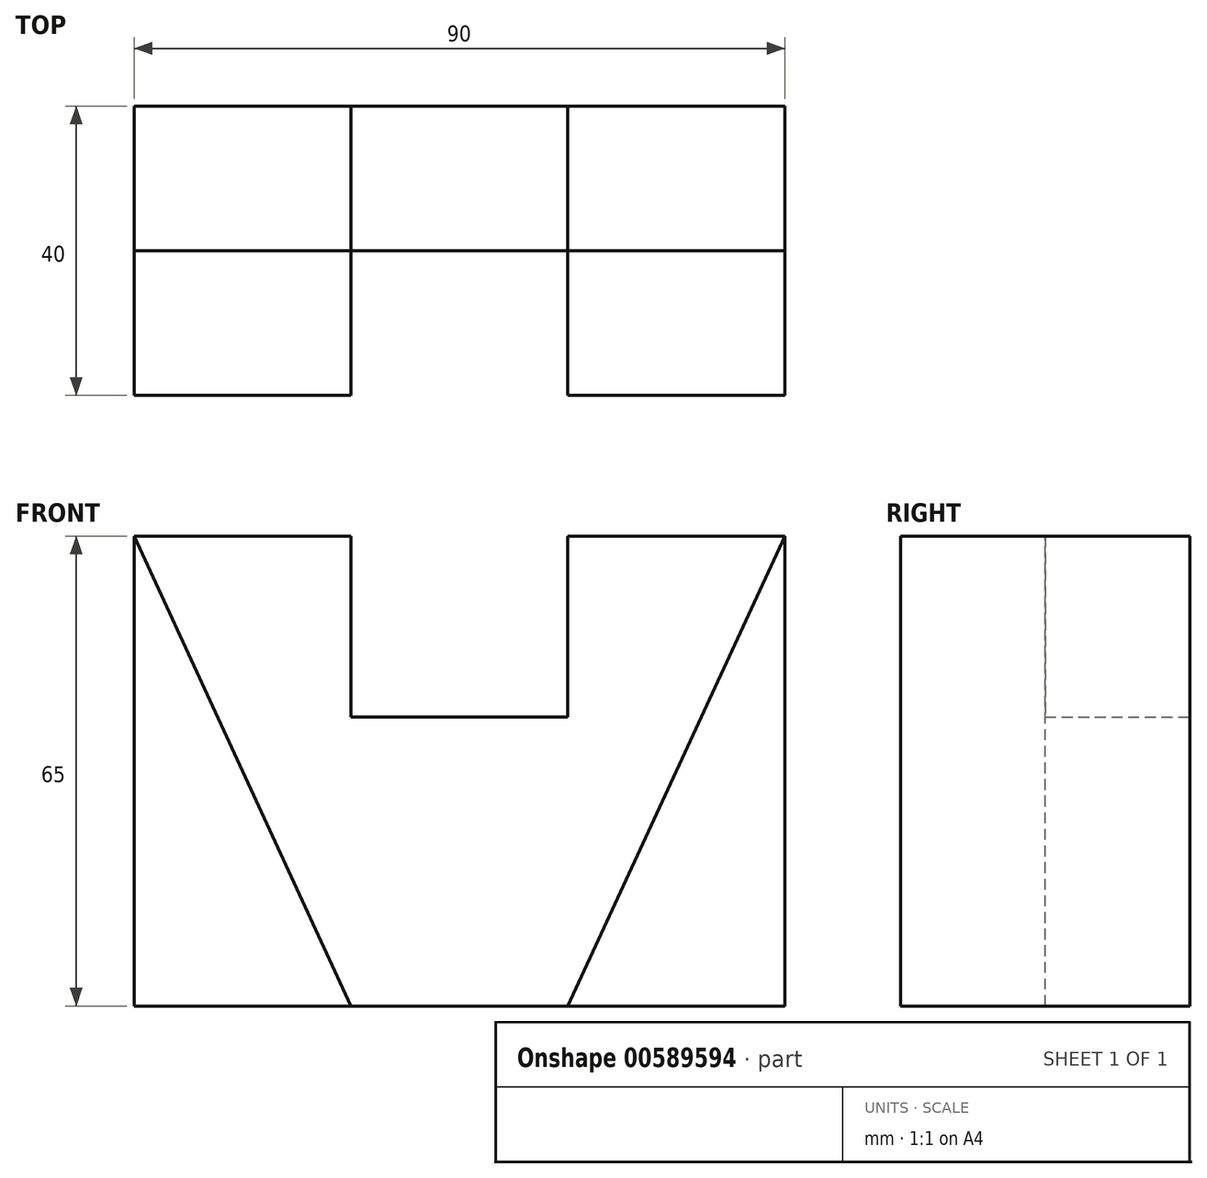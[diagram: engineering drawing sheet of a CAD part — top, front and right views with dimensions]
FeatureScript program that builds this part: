
annotation { "Feature Type Name" : "Feature", "Feature Type Description" : "" }
export const myFeature = defineFeature(function(context is Context, id is Id, definition is map)
    precondition{}
    {
        {
            var Q0;
            Q0=qCreatedBy(makeId("Front.planeOp"),FACE);
            var sketch = newSketch(context, id + "F0", { "sketchPlane" : qUnion([Q0])});
            skLineSegment(sketch, "E0", {"start": v(-45, -30.12) * mm, "end": v(0, -30.12) * mm});
            skLineSegment(sketch, "E1", {"start": v(0, -30.12) * mm, "end": v(45, -30.12) * mm});
            skLineSegment(sketch, "E2", {"start": v(45, -30.12) * mm, "end": v(45, 34.88) * mm});
            skLineSegment(sketch, "E3", {"start": v(-45, -30.12) * mm, "end": v(-45, 34.88) * mm});
            skLineSegment(sketch, "E4", {"start": v(-45, 34.88) * mm, "end": v(-15, 34.88) * mm});
            skLineSegment(sketch, "E5", {"start": v(45, 34.88) * mm, "end": v(15, 34.88) * mm});
            skLineSegment(sketch, "E6", {"start": v(-15, 34.88) * mm, "end": v(-15, 9.88) * mm});
            skLineSegment(sketch, "E7", {"start": v(15, 34.88) * mm, "end": v(15, 9.88) * mm});
            skLineSegment(sketch, "E8", {"start": v(-15, 9.88) * mm, "end": v(15, 9.88) * mm});
            skSolve(sketch);
        }
        {
            var Q0;
            Q0 = qSketchRegion(id + "F0", true);
            extrude(context, id + "F1", {"entities" : qUnion([Q0]), "depth" : 20 * mm, "offsetDistance" : 25 * mm});
        }
        {
            var Q0;
            Q0=makeQuery(id+"F1.opExtrude","CAP_FACE",FACE,{"disambiguationData":[OSD([sQuery(id+"F0.wireOp",EDGE,"E0"),sQuery(id+"F0.wireOp",EDGE,"E1"),sQuery(id+"F0.wireOp",EDGE,"E2"),sQuery(id+"F0.wireOp",EDGE,"E3"),sQuery(id+"F0.wireOp",EDGE,"E4"),sQuery(id+"F0.wireOp",EDGE,"E5"),sQuery(id+"F0.wireOp",EDGE,"E6"),sQuery(id+"F0.wireOp",EDGE,"E7"),sQuery(id+"F0.wireOp",EDGE,"E8")])],"isStart":false});
            var sketch = newSketch(context, id + "F2", { "sketchPlane" : qUnion([Q0])});
            skLineSegment(sketch, "E9", {"start": v(-45, -30.12) * mm, "end": v(-15, -30.12) * mm});
            skLineSegment(sketch, "E10", {"start": v(-15, -30.12) * mm, "end": v(-45, 34.88) * mm});
            skLineSegment(sketch, "E11", {"start": v(45, -30.12) * mm, "end": v(15, -30.12) * mm});
            skLineSegment(sketch, "E12", {"start": v(15, -30.12) * mm, "end": v(45, 34.88) * mm});
            skSolve(sketch);
        }
        {
            var Q0;
            Q0 = qSketchRegion(id + "F2", true);
            var Q1;
            Q1=makeQuery(id+"F2.imprint","IMPRINT",FACE,{"disambiguationData":[TD([[makeQuery(id+"F2.imprint","IMPRINT",EDGE,{"derivedFrom":sQuery(id+"F2.wireOp",EDGE,"E9")}),1.0]])]});
            var Q2;
            Q2=makeQuery(id+"F2.imprint","IMPRINT",FACE,{"disambiguationData":[TD([[makeQuery(id+"F2.imprint","IMPRINT",EDGE,{"derivedFrom":sQuery(id+"F2.wireOp",EDGE,"E11")}),1.0]])]});
            extrude(context, id + "F3", {"entities" : qUnion([Q0, Q1, Q2]), "operationType" : NewBodyOperationType.ADD, "depth" : 20 * mm, "offsetDistance" : 25 * mm});
        }
    });
